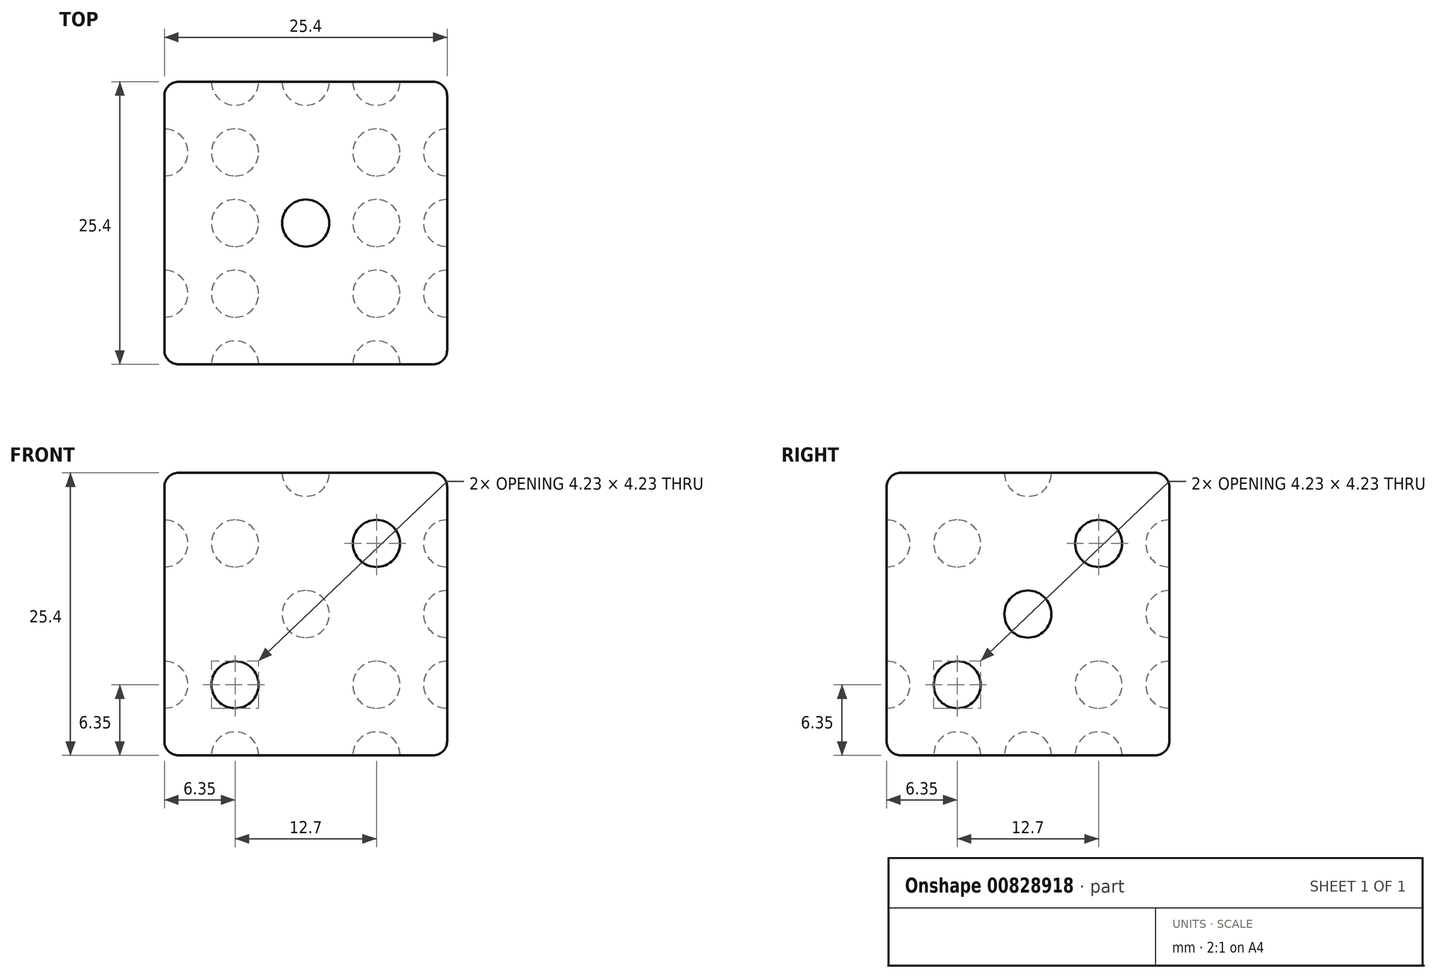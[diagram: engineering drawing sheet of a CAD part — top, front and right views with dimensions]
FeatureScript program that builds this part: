
annotation { "Feature Type Name" : "Feature", "Feature Type Description" : "" }
export const myFeature = defineFeature(function(context is Context, id is Id, definition is map)
    precondition{}
    {
        {
            var Q0;
            Q0=qCreatedBy(makeId("Top.planeOp"),FACE);
            var sketch = newSketch(context, id + "F0", { "sketchPlane" : qUnion([Q0])});
            skLineSegment(sketch, "E0.bottom", {"start": v(12.7, 12.7) * mm, "end": v(-12.7, 12.7) * mm});
            skLineSegment(sketch, "E0.top", {"start": v(12.7, -12.7) * mm, "end": v(-12.7, -12.7) * mm});
            skLineSegment(sketch, "E0.left", {"start": v(12.7, 12.7) * mm, "end": v(12.7, -12.7) * mm});
            skLineSegment(sketch, "E0.right", {"start": v(-12.7, 12.7) * mm, "end": v(-12.7, -12.7) * mm});
            skPoint(sketch, "E0.middle", {"position": v(0, 0) * mm});
            skSolve(sketch);
        }
        {
            var Q0;
            Q0 = qSketchRegion(id + "F0", true);
            extrude(context, id + "F1", {"entities" : qUnion([Q0]), "depth" : 25.4 * mm, "offsetDistance" : 25.4 * mm});
        }
        {
            var Q0;
            Q0=makeQuery(id+"F1.opExtrude","CAP_FACE",FACE,{"disambiguationData":[OSD([sQuery(id+"F0.wireOp",EDGE,"E0.bottom"),sQuery(id+"F0.wireOp",EDGE,"E0.top"),sQuery(id+"F0.wireOp",EDGE,"E0.left"),sQuery(id+"F0.wireOp",EDGE,"E0.right")])],"isStart":false});
            var sketch = newSketch(context, id + "F2", { "sketchPlane" : qUnion([Q0])});
            skLineSegment(sketch, "E1", {"start": v(-4.23, 12.7) * mm, "end": v(-4.23, -12.7) * mm, "construction": true});
            skLineSegment(sketch, "E2", {"start": v(4.23, 12.7) * mm, "end": v(4.23, -12.7) * mm, "construction": true});
            skLineSegment(sketch, "E3", {"start": v(-12.7, 4.23) * mm, "end": v(12.7, 4.23) * mm, "construction": true});
            skLineSegment(sketch, "E4", {"start": v(-12.7, -4.23) * mm, "end": v(12.7, -4.23) * mm, "construction": true});
            skLineSegment(sketch, "E5", {"start": v(0, 12.7) * mm, "end": v(0, -12.7) * mm, "construction": true});
            skArc(sketch, "E6", {"start": v(0, -2.12) * mm, "mid": v(2.12, 0) * mm, "end": v(0, 2.12) * mm});
            skLineSegment(sketch, "E7", {"start": v(0, 2.12) * mm, "end": v(0, -2.12) * mm});
            skSolve(sketch);
        }
        {
            var Q0;
            Q0=makeQuery(id+"F2.imprint","IMPRINT",FACE,{"disambiguationData":[TD([[makeQuery(id+"F2.imprint","IMPRINT",EDGE,{"derivedFrom":sQuery(id+"F2.wireOp",EDGE,"E6")}),1.0]])]});
            var Q1;
            Q1=sQuery(id+"F2.wireOp",EDGE,"E7");
            revolve(context, id + "F3", {"operationType" : NewBodyOperationType.REMOVE, "surfaceOperationType" : NewSurfaceOperationType.NEW, "entities" : qUnion([Q0]), "axis" : qUnion([Q1]), "revolveType" : RevolveType.FULL, "oppositeDirection" : true});
        }
        {
            var Q0;
            Q0=makeQuery(id+"F1.opExtrude","SWEPT_FACE",FACE,{"disambiguationData":[OSD([sQuery(id+"F0.wireOp",EDGE,"E0.top")])]});
            var sketch = newSketch(context, id + "F4", { "sketchPlane" : qUnion([Q0])});
            skLineSegment(sketch, "E8", {"start": v(-6.35, 25.4) * mm, "end": v(-6.35, 0) * mm, "construction": true});
            skLineSegment(sketch, "E9", {"start": v(0, 25.4) * mm, "end": v(0, 0) * mm, "construction": true});
            skLineSegment(sketch, "E10", {"start": v(6.35, 25.4) * mm, "end": v(6.35, 0) * mm, "construction": true});
            skLineSegment(sketch, "E11", {"start": v(12.7, 19.05) * mm, "end": v(-12.7, 19.05) * mm, "construction": true});
            skLineSegment(sketch, "E12", {"start": v(-12.7, 12.7) * mm, "end": v(12.7, 12.7) * mm, "construction": true});
            skLineSegment(sketch, "E13", {"start": v(12.7, 6.35) * mm, "end": v(-12.7, 6.35) * mm, "construction": true});
            skPoint(sketch, "E14", {"position": v(6.35, 19.05) * mm});
            skPoint(sketch, "E15", {"position": v(-6.35, 6.35) * mm});
            skArc(sketch, "E16", {"start": v(6.35, 16.93) * mm, "mid": v(8.47, 19.05) * mm, "end": v(6.35, 21.17) * mm});
            skArc(sketch, "E17", {"start": v(-6.35, 4.23) * mm, "mid": v(-4.23, 6.35) * mm, "end": v(-6.35, 8.47) * mm});
            skLineSegment(sketch, "E18", {"start": v(6.35, 21.17) * mm, "end": v(6.35, 16.93) * mm});
            skLineSegment(sketch, "E19", {"start": v(-6.35, 8.47) * mm, "end": v(-6.35, 4.23) * mm});
            skSolve(sketch);
        }
        {
            var Q0;
            Q0=makeQuery(id+"F4.imprint","IMPRINT",FACE,{"disambiguationData":[TD([[makeQuery(id+"F4.imprint","IMPRINT",EDGE,{"derivedFrom":sQuery(id+"F4.wireOp",EDGE,"E17")}),1.0]])]});
            var Q1;
            Q1=sQuery(id+"F4.wireOp",EDGE,"E19");
            revolve(context, id + "F5", {"operationType" : NewBodyOperationType.REMOVE, "surfaceOperationType" : NewSurfaceOperationType.NEW, "entities" : qUnion([Q0]), "axis" : qUnion([Q1]), "revolveType" : RevolveType.FULL, "oppositeDirection" : true});
        }
        {
            var Q0;
            Q0=makeQuery(id+"F4.imprint","IMPRINT",FACE,{"disambiguationData":[TD([[makeQuery(id+"F4.imprint","IMPRINT",EDGE,{"derivedFrom":sQuery(id+"F4.wireOp",EDGE,"E16")}),1.0]])]});
            var Q1;
            Q1=sQuery(id+"F4.wireOp",EDGE,"E18");
            revolve(context, id + "F6", {"operationType" : NewBodyOperationType.REMOVE, "surfaceOperationType" : NewSurfaceOperationType.NEW, "entities" : qUnion([Q0]), "axis" : qUnion([Q1]), "revolveType" : RevolveType.FULL, "oppositeDirection" : true});
        }
        {
            var Q0;
            Q0=makeQuery(id+"F1.opExtrude","SWEPT_FACE",FACE,{"disambiguationData":[OSD([sQuery(id+"F0.wireOp",EDGE,"E0.left")])]});
            var sketch = newSketch(context, id + "F7", { "sketchPlane" : qUnion([Q0])});
            skLineSegment(sketch, "E20", {"start": v(-6.35, 25.4) * mm, "end": v(-6.35, 0) * mm, "construction": true});
            skLineSegment(sketch, "E21", {"start": v(0, 25.4) * mm, "end": v(0, 0) * mm, "construction": true});
            skLineSegment(sketch, "E22", {"start": v(6.35, 25.4) * mm, "end": v(6.35, 0) * mm, "construction": true});
            skLineSegment(sketch, "E23", {"start": v(12.7, 19.05) * mm, "end": v(-12.7, 19.05) * mm, "construction": true});
            skLineSegment(sketch, "E24", {"start": v(12.7, 12.7) * mm, "end": v(-12.7, 12.7) * mm, "construction": true});
            skLineSegment(sketch, "E25", {"start": v(12.7, 6.35) * mm, "end": v(-12.7, 6.35) * mm, "construction": true});
            skPoint(sketch, "E26", {"position": v(6.35, 19.05) * mm});
            skPoint(sketch, "E27", {"position": v(0, 12.7) * mm});
            skPoint(sketch, "E28", {"position": v(-6.35, 6.35) * mm});
            skArc(sketch, "E29", {"start": v(6.35, 16.93) * mm, "mid": v(8.47, 19.05) * mm, "end": v(6.35, 21.17) * mm});
            skArc(sketch, "E30", {"start": v(0, 10.58) * mm, "mid": v(2.12, 12.7) * mm, "end": v(0, 14.82) * mm});
            skArc(sketch, "E31", {"start": v(-6.35, 4.23) * mm, "mid": v(-4.23, 6.35) * mm, "end": v(-6.35, 8.47) * mm});
            skLineSegment(sketch, "E32", {"start": v(6.35, 21.17) * mm, "end": v(6.35, 16.93) * mm});
            skLineSegment(sketch, "E33", {"start": v(0, 14.82) * mm, "end": v(0, 10.58) * mm});
            skLineSegment(sketch, "E34", {"start": v(-6.35, 8.47) * mm, "end": v(-6.35, 4.23) * mm});
            skSolve(sketch);
        }
        {
            var Q0;
            Q0=makeQuery(id+"F7.imprint","IMPRINT",FACE,{"disambiguationData":[TD([[makeQuery(id+"F7.imprint","IMPRINT",EDGE,{"derivedFrom":sQuery(id+"F7.wireOp",EDGE,"E29")}),1.0]])]});
            var Q1;
            Q1=sQuery(id+"F7.wireOp",EDGE,"E32");
            revolve(context, id + "F8", {"operationType" : NewBodyOperationType.REMOVE, "surfaceOperationType" : NewSurfaceOperationType.NEW, "entities" : qUnion([Q0]), "axis" : qUnion([Q1]), "revolveType" : RevolveType.FULL, "oppositeDirection" : true});
        }
        {
            var Q0;
            Q0=makeQuery(id+"F7.imprint","IMPRINT",FACE,{"disambiguationData":[TD([[makeQuery(id+"F7.imprint","IMPRINT",EDGE,{"derivedFrom":sQuery(id+"F7.wireOp",EDGE,"E30")}),1.0]])]});
            var Q1;
            Q1=sQuery(id+"F7.wireOp",EDGE,"E33");
            revolve(context, id + "F9", {"operationType" : NewBodyOperationType.REMOVE, "surfaceOperationType" : NewSurfaceOperationType.NEW, "entities" : qUnion([Q0]), "axis" : qUnion([Q1]), "revolveType" : RevolveType.FULL, "oppositeDirection" : true});
        }
        {
            var Q0;
            Q0=makeQuery(id+"F7.imprint","IMPRINT",FACE,{"disambiguationData":[TD([[makeQuery(id+"F7.imprint","IMPRINT",EDGE,{"derivedFrom":sQuery(id+"F7.wireOp",EDGE,"E31")}),1.0]])]});
            var Q1;
            Q1=sQuery(id+"F7.wireOp",EDGE,"E34");
            revolve(context, id + "F10", {"operationType" : NewBodyOperationType.REMOVE, "surfaceOperationType" : NewSurfaceOperationType.NEW, "entities" : qUnion([Q0]), "axis" : qUnion([Q1]), "revolveType" : RevolveType.FULL, "oppositeDirection" : true});
        }
        {
            var Q0;
            Q0=makeQuery(id+"F1.opExtrude","SWEPT_FACE",FACE,{"disambiguationData":[OSD([sQuery(id+"F0.wireOp",EDGE,"E0.right")])]});
            var sketch = newSketch(context, id + "F11", { "sketchPlane" : qUnion([Q0])});
            skLineSegment(sketch, "E35", {"start": v(-6.35, 25.4) * mm, "end": v(-6.35, 0) * mm, "construction": true});
            skLineSegment(sketch, "E36", {"start": v(0, 25.4) * mm, "end": v(0, 0) * mm, "construction": true});
            skLineSegment(sketch, "E37", {"start": v(6.35, 25.4) * mm, "end": v(6.35, 0) * mm, "construction": true});
            skLineSegment(sketch, "E38", {"start": v(12.7, 19.05) * mm, "end": v(-12.7, 19.05) * mm, "construction": true});
            skLineSegment(sketch, "E39", {"start": v(12.7, 12.7) * mm, "end": v(-12.7, 12.7) * mm, "construction": true});
            skLineSegment(sketch, "E40", {"start": v(12.7, 6.35) * mm, "end": v(-12.7, 6.35) * mm, "construction": true});
            skPoint(sketch, "E41", {"position": v(-6.35, 19.05) * mm});
            skPoint(sketch, "E42", {"position": v(6.35, 19.05) * mm});
            skPoint(sketch, "E43", {"position": v(6.35, 6.35) * mm});
            skPoint(sketch, "E44", {"position": v(-6.35, 6.35) * mm});
            skLineSegment(sketch, "E45", {"start": v(-6.35, 19.05) * mm, "end": v(-6.35, 21.17) * mm});
            skLineSegment(sketch, "E46", {"start": v(-6.35, 19.05) * mm, "end": v(-6.35, 16.93) * mm});
            skLineSegment(sketch, "E47", {"start": v(6.35, 19.05) * mm, "end": v(6.35, 21.17) * mm});
            skLineSegment(sketch, "E48", {"start": v(6.35, 19.05) * mm, "end": v(6.35, 16.93) * mm});
            skLineSegment(sketch, "E49", {"start": v(-6.35, 6.35) * mm, "end": v(-6.35, 8.47) * mm});
            skLineSegment(sketch, "E50", {"start": v(-6.35, 6.35) * mm, "end": v(-6.35, 4.23) * mm});
            skLineSegment(sketch, "E51", {"start": v(6.35, 6.35) * mm, "end": v(6.35, 8.47) * mm});
            skLineSegment(sketch, "E52", {"start": v(6.35, 6.35) * mm, "end": v(6.35, 4.23) * mm});
            skArc(sketch, "E53", {"start": v(-6.35, 16.93) * mm, "mid": v(-4.23, 19.05) * mm, "end": v(-6.35, 21.17) * mm});
            skArc(sketch, "E54", {"start": v(6.35, 16.93) * mm, "mid": v(8.47, 19.05) * mm, "end": v(6.35, 21.17) * mm});
            skArc(sketch, "E55", {"start": v(-6.35, 4.23) * mm, "mid": v(-4.23, 6.35) * mm, "end": v(-6.35, 8.47) * mm});
            skArc(sketch, "E56", {"start": v(6.35, 4.23) * mm, "mid": v(8.47, 6.35) * mm, "end": v(6.35, 8.47) * mm});
            skSolve(sketch);
        }
        {
            var Q0;
            Q0=makeQuery(id+"F11.imprint","IMPRINT",FACE,{"disambiguationData":[TD([[makeQuery(id+"F11.imprint","IMPRINT",EDGE,{"derivedFrom":sQuery(id+"F11.wireOp",EDGE,"E45")}),-1.0]])]});
            var Q1;
            Q1=sQuery(id+"F11.wireOp",EDGE,"E46");
            revolve(context, id + "F12", {"operationType" : NewBodyOperationType.REMOVE, "surfaceOperationType" : NewSurfaceOperationType.NEW, "entities" : qUnion([Q0]), "axis" : qUnion([Q1]), "revolveType" : RevolveType.FULL, "oppositeDirection" : true});
        }
        {
            var Q0;
            Q0=makeQuery(id+"F11.imprint","IMPRINT",FACE,{"disambiguationData":[TD([[makeQuery(id+"F11.imprint","IMPRINT",EDGE,{"derivedFrom":sQuery(id+"F11.wireOp",EDGE,"E47")}),-1.0]])]});
            var Q1;
            Q1=sQuery(id+"F11.wireOp",EDGE,"E48");
            revolve(context, id + "F13", {"operationType" : NewBodyOperationType.REMOVE, "surfaceOperationType" : NewSurfaceOperationType.NEW, "entities" : qUnion([Q0]), "axis" : qUnion([Q1]), "revolveType" : RevolveType.FULL, "oppositeDirection" : true});
        }
        {
            var Q0;
            Q0=makeQuery(id+"F11.imprint","IMPRINT",FACE,{"disambiguationData":[TD([[makeQuery(id+"F11.imprint","IMPRINT",EDGE,{"derivedFrom":sQuery(id+"F11.wireOp",EDGE,"E49")}),-1.0]])]});
            var Q1;
            Q1=sQuery(id+"F11.wireOp",EDGE,"E50");
            revolve(context, id + "F14", {"operationType" : NewBodyOperationType.REMOVE, "surfaceOperationType" : NewSurfaceOperationType.NEW, "entities" : qUnion([Q0]), "axis" : qUnion([Q1]), "revolveType" : RevolveType.FULL, "oppositeDirection" : true});
        }
        {
            var Q0;
            Q0=makeQuery(id+"F11.imprint","IMPRINT",FACE,{"disambiguationData":[TD([[makeQuery(id+"F11.imprint","IMPRINT",EDGE,{"derivedFrom":sQuery(id+"F11.wireOp",EDGE,"E51")}),-1.0]])]});
            var Q1;
            Q1=sQuery(id+"F11.wireOp",EDGE,"E52");
            revolve(context, id + "F15", {"operationType" : NewBodyOperationType.REMOVE, "surfaceOperationType" : NewSurfaceOperationType.NEW, "entities" : qUnion([Q0]), "axis" : qUnion([Q1]), "revolveType" : RevolveType.FULL, "oppositeDirection" : true});
        }
        {
            var Q0;
            Q0=makeQuery(id+"F1.opExtrude","SWEPT_FACE",FACE,{"disambiguationData":[OSD([sQuery(id+"F0.wireOp",EDGE,"E0.bottom")])]});
            var sketch = newSketch(context, id + "F16", { "sketchPlane" : qUnion([Q0])});
            skLineSegment(sketch, "E57", {"start": v(-6.35, 25.4) * mm, "end": v(-6.35, 0) * mm, "construction": true});
            skLineSegment(sketch, "E58", {"start": v(0, 25.4) * mm, "end": v(0, 0) * mm, "construction": true});
            skLineSegment(sketch, "E59", {"start": v(6.35, 25.4) * mm, "end": v(6.35, 0) * mm, "construction": true});
            skLineSegment(sketch, "E60", {"start": v(12.7, 19.05) * mm, "end": v(-12.7, 19.05) * mm, "construction": true});
            skLineSegment(sketch, "E61", {"start": v(12.7, 12.7) * mm, "end": v(-12.7, 12.7) * mm, "construction": true});
            skLineSegment(sketch, "E62", {"start": v(12.7, 6.35) * mm, "end": v(-12.7, 6.35) * mm, "construction": true});
            skPoint(sketch, "E63", {"position": v(-6.35, 19.05) * mm});
            skPoint(sketch, "E64", {"position": v(6.35, 19.05) * mm});
            skPoint(sketch, "E65", {"position": v(0, 12.7) * mm});
            skPoint(sketch, "E66", {"position": v(-6.35, 6.35) * mm});
            skPoint(sketch, "E67", {"position": v(6.35, 6.35) * mm});
            skArc(sketch, "E68", {"start": v(-6.35, 16.93) * mm, "mid": v(-4.23, 19.05) * mm, "end": v(-6.35, 21.17) * mm});
            skArc(sketch, "E69", {"start": v(0, 10.58) * mm, "mid": v(2.12, 12.7) * mm, "end": v(0, 14.82) * mm});
            skLineSegment(sketch, "E70", {"start": v(-6.35, 21.17) * mm, "end": v(-6.35, 16.93) * mm});
            skLineSegment(sketch, "E71", {"start": v(6.35, 21.17) * mm, "end": v(6.35, 16.93) * mm});
            skLineSegment(sketch, "E72", {"start": v(0, 14.82) * mm, "end": v(0, 10.58) * mm});
            skLineSegment(sketch, "E73", {"start": v(-6.35, 8.47) * mm, "end": v(-6.35, 4.23) * mm});
            skLineSegment(sketch, "E74", {"start": v(6.35, 8.47) * mm, "end": v(6.35, 4.23) * mm});
            skArc(sketch, "E75", {"start": v(6.35, 16.93) * mm, "mid": v(8.47, 19.05) * mm, "end": v(6.35, 21.17) * mm});
            skArc(sketch, "E76", {"start": v(-6.35, 4.23) * mm, "mid": v(-4.23, 6.35) * mm, "end": v(-6.35, 8.47) * mm});
            skArc(sketch, "E77", {"start": v(6.35, 4.23) * mm, "mid": v(8.47, 6.35) * mm, "end": v(6.35, 8.47) * mm});
            skSolve(sketch);
        }
        {
            var Q0;
            Q0=makeQuery(id+"F16.imprint","IMPRINT",FACE,{"disambiguationData":[TD([[makeQuery(id+"F16.imprint","IMPRINT",EDGE,{"derivedFrom":sQuery(id+"F16.wireOp",EDGE,"E68")}),1.0]])]});
            var Q1;
            Q1=sQuery(id+"F16.wireOp",EDGE,"E70");
            revolve(context, id + "F17", {"operationType" : NewBodyOperationType.REMOVE, "surfaceOperationType" : NewSurfaceOperationType.NEW, "entities" : qUnion([Q0]), "axis" : qUnion([Q1]), "revolveType" : RevolveType.FULL, "oppositeDirection" : true});
        }
        {
            var Q0;
            Q0=makeQuery(id+"F16.imprint","IMPRINT",FACE,{"disambiguationData":[TD([[makeQuery(id+"F16.imprint","IMPRINT",EDGE,{"derivedFrom":sQuery(id+"F16.wireOp",EDGE,"E71")}),1.0]])]});
            var Q1;
            Q1=sQuery(id+"F16.wireOp",EDGE,"E71");
            revolve(context, id + "F18", {"operationType" : NewBodyOperationType.REMOVE, "surfaceOperationType" : NewSurfaceOperationType.NEW, "entities" : qUnion([Q0]), "axis" : qUnion([Q1]), "revolveType" : RevolveType.FULL, "oppositeDirection" : true});
        }
        {
            var Q0;
            Q0=makeQuery(id+"F16.imprint","IMPRINT",FACE,{"disambiguationData":[TD([[makeQuery(id+"F16.imprint","IMPRINT",EDGE,{"derivedFrom":sQuery(id+"F16.wireOp",EDGE,"E69")}),1.0]])]});
            var Q1;
            Q1=sQuery(id+"F16.wireOp",EDGE,"E72");
            revolve(context, id + "F19", {"operationType" : NewBodyOperationType.REMOVE, "surfaceOperationType" : NewSurfaceOperationType.NEW, "entities" : qUnion([Q0]), "axis" : qUnion([Q1]), "revolveType" : RevolveType.FULL, "oppositeDirection" : true});
        }
        {
            var Q0;
            Q0=makeQuery(id+"F16.imprint","IMPRINT",FACE,{"disambiguationData":[TD([[makeQuery(id+"F16.imprint","IMPRINT",EDGE,{"derivedFrom":sQuery(id+"F16.wireOp",EDGE,"E73")}),1.0]])]});
            var Q1;
            Q1=sQuery(id+"F16.wireOp",EDGE,"E73");
            revolve(context, id + "F20", {"operationType" : NewBodyOperationType.REMOVE, "surfaceOperationType" : NewSurfaceOperationType.NEW, "entities" : qUnion([Q0]), "axis" : qUnion([Q1]), "revolveType" : RevolveType.FULL, "oppositeDirection" : true});
        }
        {
            var Q0;
            Q0=makeQuery(id+"F16.imprint","IMPRINT",FACE,{"disambiguationData":[TD([[makeQuery(id+"F16.imprint","IMPRINT",EDGE,{"derivedFrom":sQuery(id+"F16.wireOp",EDGE,"E74")}),1.0]])]});
            var Q1;
            Q1=sQuery(id+"F16.wireOp",EDGE,"E74");
            revolve(context, id + "F21", {"operationType" : NewBodyOperationType.REMOVE, "surfaceOperationType" : NewSurfaceOperationType.NEW, "entities" : qUnion([Q0]), "axis" : qUnion([Q1]), "revolveType" : RevolveType.FULL, "oppositeDirection" : true});
        }
        {
            var Q0;
            Q0=makeQuery(id+"F1.opExtrude","CAP_FACE",FACE,{"disambiguationData":[OSD([sQuery(id+"F0.wireOp",EDGE,"E0.bottom"),sQuery(id+"F0.wireOp",EDGE,"E0.top"),sQuery(id+"F0.wireOp",EDGE,"E0.left"),sQuery(id+"F0.wireOp",EDGE,"E0.right")])],"isStart":true});
            var sketch = newSketch(context, id + "F22", { "sketchPlane" : qUnion([Q0])});
            skLineSegment(sketch, "E78", {"start": v(-6.35, 12.7) * mm, "end": v(-6.35, -12.7) * mm, "construction": true});
            skLineSegment(sketch, "E79", {"start": v(0, 12.7) * mm, "end": v(0, -12.7) * mm, "construction": true});
            skLineSegment(sketch, "E80", {"start": v(6.35, 12.7) * mm, "end": v(6.35, -12.7) * mm, "construction": true});
            skLineSegment(sketch, "E81", {"start": v(12.7, 6.35) * mm, "end": v(-12.7, 6.35) * mm, "construction": true});
            skLineSegment(sketch, "E82", {"start": v(12.7, 0) * mm, "end": v(-12.7, 0) * mm, "construction": true});
            skLineSegment(sketch, "E83", {"start": v(12.7, -6.35) * mm, "end": v(-12.7, -6.35) * mm, "construction": true});
            skPoint(sketch, "E84", {"position": v(-6.35, 6.35) * mm});
            skPoint(sketch, "E85", {"position": v(6.35, 6.35) * mm});
            skPoint(sketch, "E86", {"position": v(6.35, 0) * mm});
            skPoint(sketch, "E87", {"position": v(-6.35, 0) * mm});
            skPoint(sketch, "E88", {"position": v(-6.35, -6.35) * mm});
            skPoint(sketch, "E89", {"position": v(6.35, -6.35) * mm});
            skArc(sketch, "E90", {"start": v(-6.35, 4.23) * mm, "mid": v(-4.23, 6.35) * mm, "end": v(-6.35, 8.47) * mm});
            skArc(sketch, "E91", {"start": v(6.35, 4.23) * mm, "mid": v(8.47, 6.35) * mm, "end": v(6.35, 8.47) * mm});
            skArc(sketch, "E92", {"start": v(-6.35, -2.12) * mm, "mid": v(-4.23, 0) * mm, "end": v(-6.35, 2.12) * mm});
            skArc(sketch, "E93", {"start": v(6.35, -2.12) * mm, "mid": v(8.47, 0) * mm, "end": v(6.35, 2.12) * mm});
            skArc(sketch, "E94", {"start": v(-6.35, -8.47) * mm, "mid": v(-4.23, -6.35) * mm, "end": v(-6.35, -4.23) * mm});
            skArc(sketch, "E95", {"start": v(6.35, -8.47) * mm, "mid": v(8.47, -6.35) * mm, "end": v(6.35, -4.23) * mm});
            skLineSegment(sketch, "E96", {"start": v(-6.35, 8.47) * mm, "end": v(-6.35, 4.23) * mm});
            skLineSegment(sketch, "E97", {"start": v(6.35, 8.47) * mm, "end": v(6.35, 4.23) * mm});
            skLineSegment(sketch, "E98", {"start": v(-6.35, 2.12) * mm, "end": v(-6.35, -2.12) * mm});
            skLineSegment(sketch, "E99", {"start": v(6.35, 2.12) * mm, "end": v(6.35, -2.12) * mm});
            skLineSegment(sketch, "E100", {"start": v(-6.35, -4.23) * mm, "end": v(-6.35, -8.47) * mm});
            skLineSegment(sketch, "E101", {"start": v(6.35, -4.23) * mm, "end": v(6.35, -8.47) * mm});
            skSolve(sketch);
        }
        {
            var Q0;
            Q0=makeQuery(id+"F22.imprint","IMPRINT",FACE,{"disambiguationData":[TD([[makeQuery(id+"F22.imprint","IMPRINT",EDGE,{"derivedFrom":sQuery(id+"F22.wireOp",EDGE,"E90")}),1.0]])]});
            var Q1;
            Q1=sQuery(id+"F22.wireOp",EDGE,"E96");
            revolve(context, id + "F23", {"operationType" : NewBodyOperationType.REMOVE, "surfaceOperationType" : NewSurfaceOperationType.NEW, "entities" : qUnion([Q0]), "axis" : qUnion([Q1]), "revolveType" : RevolveType.FULL, "oppositeDirection" : true});
        }
        {
            var Q0;
            Q0=makeQuery(id+"F22.imprint","IMPRINT",FACE,{"disambiguationData":[TD([[makeQuery(id+"F22.imprint","IMPRINT",EDGE,{"derivedFrom":sQuery(id+"F22.wireOp",EDGE,"E91")}),1.0]])]});
            var Q1;
            Q1=sQuery(id+"F22.wireOp",EDGE,"E97");
            revolve(context, id + "F24", {"operationType" : NewBodyOperationType.REMOVE, "surfaceOperationType" : NewSurfaceOperationType.NEW, "entities" : qUnion([Q0]), "axis" : qUnion([Q1]), "revolveType" : RevolveType.FULL, "oppositeDirection" : true});
        }
        {
            var Q0;
            Q0=makeQuery(id+"F22.imprint","IMPRINT",FACE,{"disambiguationData":[TD([[makeQuery(id+"F22.imprint","IMPRINT",EDGE,{"derivedFrom":sQuery(id+"F22.wireOp",EDGE,"E92")}),1.0]])]});
            var Q1;
            Q1=sQuery(id+"F22.wireOp",EDGE,"E98");
            revolve(context, id + "F25", {"operationType" : NewBodyOperationType.REMOVE, "surfaceOperationType" : NewSurfaceOperationType.NEW, "entities" : qUnion([Q0]), "axis" : qUnion([Q1]), "revolveType" : RevolveType.FULL, "oppositeDirection" : true});
        }
        {
            var Q0;
            Q0=makeQuery(id+"F22.imprint","IMPRINT",FACE,{"disambiguationData":[TD([[makeQuery(id+"F22.imprint","IMPRINT",EDGE,{"derivedFrom":sQuery(id+"F22.wireOp",EDGE,"E93")}),1.0]])]});
            var Q1;
            Q1=sQuery(id+"F22.wireOp",EDGE,"E99");
            revolve(context, id + "F26", {"operationType" : NewBodyOperationType.REMOVE, "surfaceOperationType" : NewSurfaceOperationType.NEW, "entities" : qUnion([Q0]), "axis" : qUnion([Q1]), "revolveType" : RevolveType.FULL, "oppositeDirection" : true});
        }
        {
            var Q0;
            Q0=makeQuery(id+"F22.imprint","IMPRINT",FACE,{"disambiguationData":[TD([[makeQuery(id+"F22.imprint","IMPRINT",EDGE,{"derivedFrom":sQuery(id+"F22.wireOp",EDGE,"E94")}),1.0]])]});
            var Q1;
            Q1=sQuery(id+"F22.wireOp",EDGE,"E100");
            revolve(context, id + "F27", {"operationType" : NewBodyOperationType.REMOVE, "surfaceOperationType" : NewSurfaceOperationType.NEW, "entities" : qUnion([Q0]), "axis" : qUnion([Q1]), "revolveType" : RevolveType.FULL, "oppositeDirection" : true});
        }
        {
            var Q0;
            Q0=makeQuery(id+"F22.imprint","IMPRINT",FACE,{"disambiguationData":[TD([[makeQuery(id+"F22.imprint","IMPRINT",EDGE,{"derivedFrom":sQuery(id+"F22.wireOp",EDGE,"E95")}),1.0]])]});
            var Q1;
            Q1=sQuery(id+"F22.wireOp",EDGE,"E101");
            revolve(context, id + "F28", {"operationType" : NewBodyOperationType.REMOVE, "surfaceOperationType" : NewSurfaceOperationType.NEW, "entities" : qUnion([Q0]), "axis" : qUnion([Q1]), "revolveType" : RevolveType.FULL, "oppositeDirection" : true});
        }
        {
            var Q0;
            Q0=makeQuery(id+"F1.opExtrude","CAP_EDGE",EDGE,{"disambiguationData":[OSD([sQuery(id+"F0.wireOp",EDGE,"E0.top")])],"isStart":false});
            var Q1;
            Q1=makeQuery(id+"F1.opExtrude","SWEPT_EDGE",EDGE,{"disambiguationData":[OSD([sQuery(id+"F0.wireOp",EDGE,"E0.top"),sQuery(id+"F0.wireOp",EDGE,"E0.left")])]});
            var Q2;
            Q2=makeQuery(id+"F1.opExtrude","CAP_EDGE",EDGE,{"disambiguationData":[OSD([sQuery(id+"F0.wireOp",EDGE,"E0.left")])],"isStart":false});
            var Q3;
            Q3=makeQuery(id+"F1.opExtrude","CAP_EDGE",EDGE,{"disambiguationData":[OSD([sQuery(id+"F0.wireOp",EDGE,"E0.left")])],"isStart":true});
            var Q4;
            Q4=makeQuery(id+"F1.opExtrude","CAP_EDGE",EDGE,{"disambiguationData":[OSD([sQuery(id+"F0.wireOp",EDGE,"E0.top")])],"isStart":true});
            var Q5;
            Q5=makeQuery(id+"F1.opExtrude","CAP_EDGE",EDGE,{"disambiguationData":[OSD([sQuery(id+"F0.wireOp",EDGE,"E0.right")])],"isStart":true});
            var Q6;
            Q6=makeQuery(id+"F1.opExtrude","SWEPT_EDGE",EDGE,{"disambiguationData":[OSD([sQuery(id+"F0.wireOp",EDGE,"E0.top"),sQuery(id+"F0.wireOp",EDGE,"E0.right")])]});
            var Q7;
            Q7=makeQuery(id+"F1.opExtrude","SWEPT_EDGE",EDGE,{"disambiguationData":[OSD([sQuery(id+"F0.wireOp",EDGE,"E0.bottom"),sQuery(id+"F0.wireOp",EDGE,"E0.right")])]});
            var Q8;
            Q8=makeQuery(id+"F1.opExtrude","CAP_EDGE",EDGE,{"disambiguationData":[OSD([sQuery(id+"F0.wireOp",EDGE,"E0.bottom")])],"isStart":true});
            var Q9;
            Q9=makeQuery(id+"F1.opExtrude","CAP_EDGE",EDGE,{"disambiguationData":[OSD([sQuery(id+"F0.wireOp",EDGE,"E0.bottom")])],"isStart":false});
            var Q10;
            Q10=makeQuery(id+"F1.opExtrude","CAP_EDGE",EDGE,{"disambiguationData":[OSD([sQuery(id+"F0.wireOp",EDGE,"E0.right")])],"isStart":false});
            var Q11;
            Q11=makeQuery(id+"F1.opExtrude","SWEPT_EDGE",EDGE,{"disambiguationData":[OSD([sQuery(id+"F0.wireOp",EDGE,"E0.bottom"),sQuery(id+"F0.wireOp",EDGE,"E0.left")])]});
            fillet(context, id + "F29", {"entities" : qUnion([Q0, Q1, Q2, Q3, Q4, Q5, Q6, Q7, Q8, Q9, Q10, Q11]), "radius" : 1.27 * mm, "tangentPropagation" : true, "allowEdgeOverflow" : false});
        }
    });
